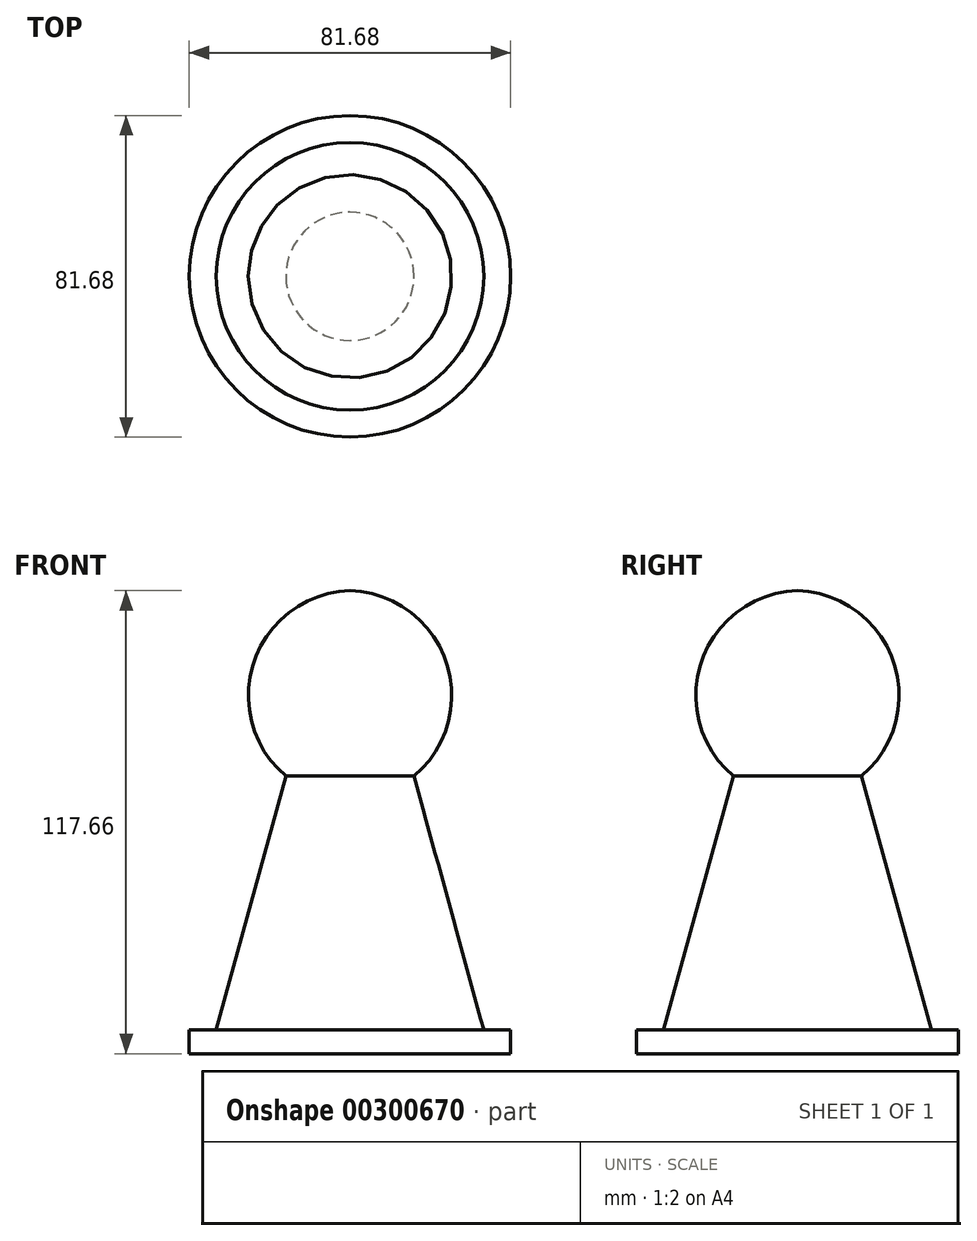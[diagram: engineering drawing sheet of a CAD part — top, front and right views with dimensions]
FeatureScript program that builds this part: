
annotation { "Feature Type Name" : "Feature", "Feature Type Description" : "" }
export const myFeature = defineFeature(function(context is Context, id is Id, definition is map)
    precondition{}
    {
        {
            var Q0;
            Q0=qCreatedBy(makeId("Front.planeOp"),FACE);
            var sketch = newSketch(context, id + "F0", { "sketchPlane" : qUnion([Q0])});
            skLineSegment(sketch, "E0", {"start": v(0, 86.24) * mm, "end": v(0, -96.52) * mm, "construction": true});
            skLineSegment(sketch, "E1", {"start": v(0, -76.25) * mm, "end": v(-40.84, -76.25) * mm});
            skLineSegment(sketch, "E2", {"start": v(-40.84, -76.25) * mm, "end": v(-40.84, -70.25) * mm});
            skLineSegment(sketch, "E3", {"start": v(-40.84, -70.25) * mm, "end": v(-33.98, -70.25) * mm});
            skLineSegment(sketch, "E4", {"start": v(-33.98, -70.25) * mm, "end": v(-16.28, -5.71) * mm});
            skArc(sketch, "E5", {"start": v(0, 41.4) * mm, "mid": v(-24.38, 23.46) * mm, "end": v(-16.28, -5.71) * mm});
            skLineSegment(sketch, "E6", {"start": v(0, 41.4) * mm, "end": v(0, -76.25) * mm});
            skSolve(sketch);
        }
        {
            var Q0;
            Q0=makeQuery(id+"F0.imprint","IMPRINT",FACE,{"disambiguationData":[TD([[makeQuery(id+"F0.imprint","IMPRINT",EDGE,{"derivedFrom":sQuery(id+"F0.wireOp",EDGE,"E1")}),-1.0]])]});
            var Q1;
            Q1=sQuery(id+"F0.wireOp",EDGE,"E0");
            revolve(context, id + "F1", {"entities" : qUnion([Q0]), "axis" : qUnion([Q1]), "revolveType" : RevolveType.FULL});
        }
    });
